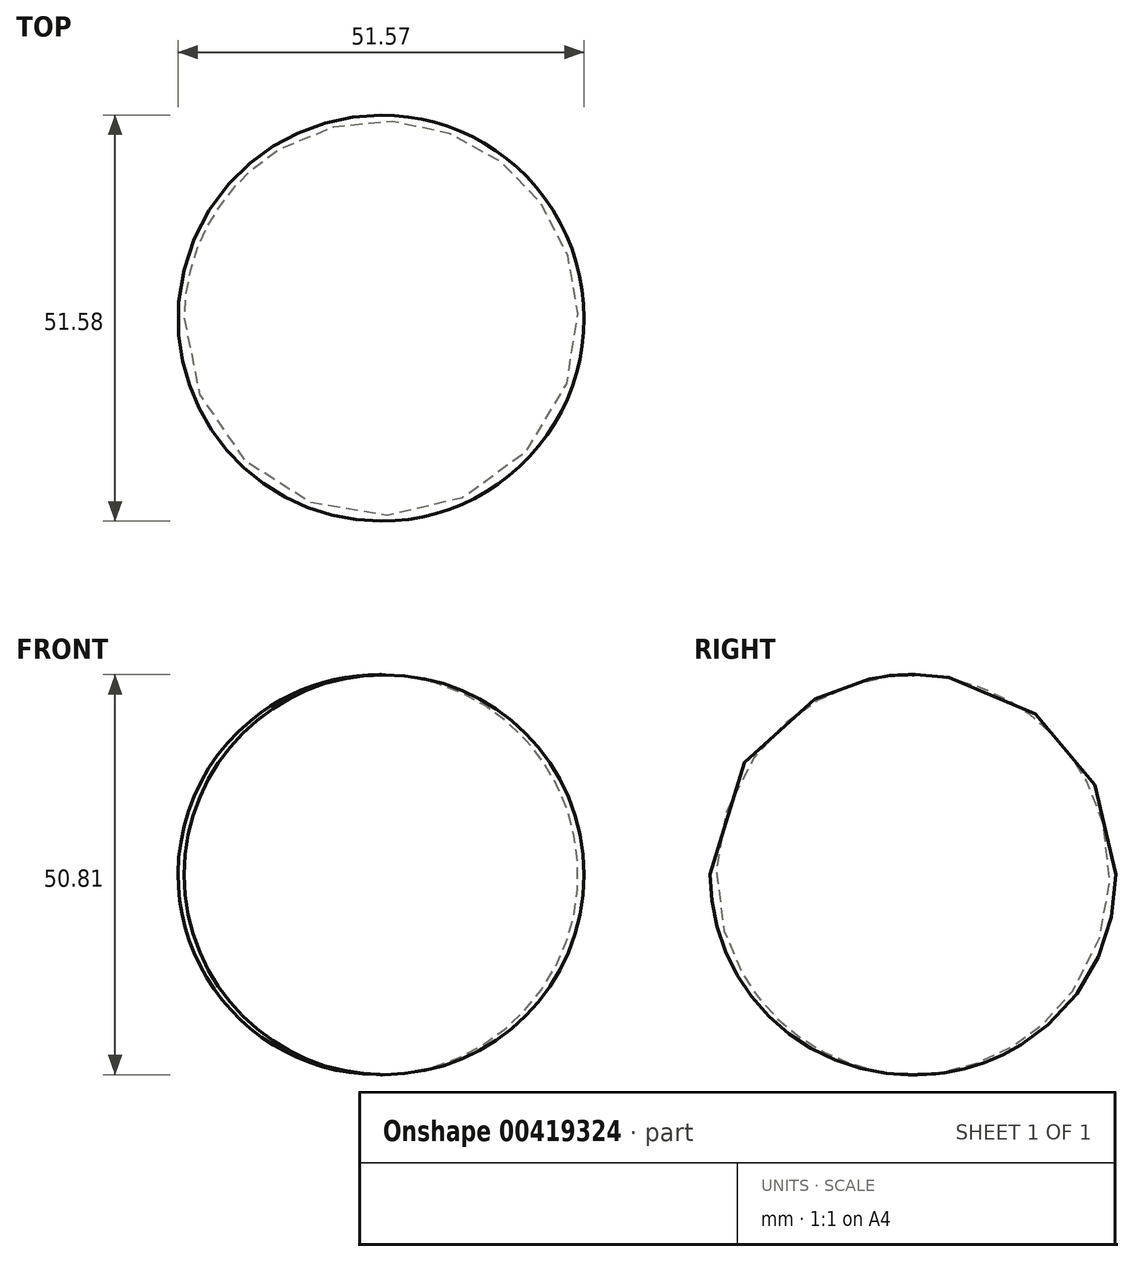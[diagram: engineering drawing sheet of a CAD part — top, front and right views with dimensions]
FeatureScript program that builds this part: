
annotation { "Feature Type Name" : "Feature", "Feature Type Description" : "" }
export const myFeature = defineFeature(function(context is Context, id is Id, definition is map)
    precondition{}
    {
        {
            var Q0;
            Q0=qCreatedBy(makeId("Front.planeOp"),FACE);
            var sketch = newSketch(context, id + "F0", { "sketchPlane" : qUnion([Q0])});
            skArc(sketch, "E0", {"start": v(0.56, 25.4) * mm, "mid": v(-25.4, 0.18) * mm, "end": v(0.2, -25.4) * mm});
            skLineSegment(sketch, "E1", {"start": v(0.56, 25.4) * mm, "end": v(0.2, -25.4) * mm});
            skSolve(sketch);
        }
        {
            var Q0;
            Q0 = qSketchRegion(id + "F0", true);
            var Q1;
            Q1=sQuery(id+"F0.wireOp",EDGE,"E1");
            revolve(context, id + "F1", {"entities" : qUnion([Q0]), "axis" : qUnion([Q1]), "revolveType" : RevolveType.FULL});
        }
    });
